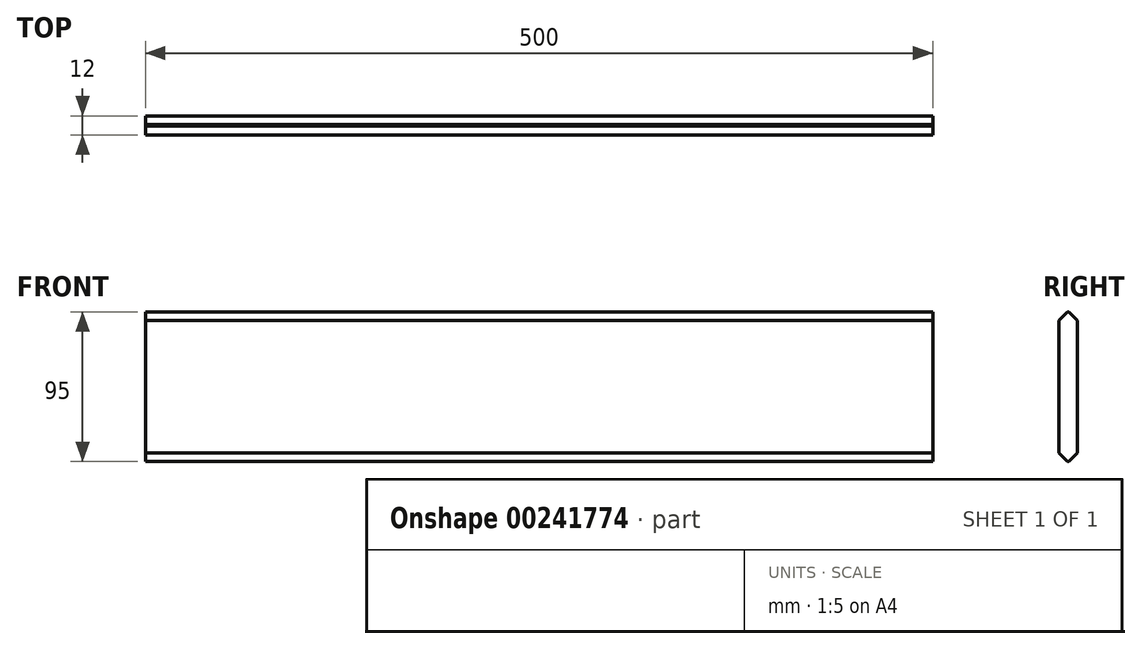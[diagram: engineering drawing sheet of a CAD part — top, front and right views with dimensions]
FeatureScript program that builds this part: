
annotation { "Feature Type Name" : "Feature", "Feature Type Description" : "" }
export const myFeature = defineFeature(function(context is Context, id is Id, definition is map)
    precondition{}
    {
        {
            var Q0;
            Q0=qCreatedBy(makeId("Front.planeOp"),FACE);
            var sketch = newSketch(context, id + "F0", { "sketchPlane" : qUnion([Q0])});
            skLineSegment(sketch, "E0.bottom", {"start": v(0, 0) * mm, "end": v(500, 0) * mm});
            skLineSegment(sketch, "E0.top", {"start": v(0, 95) * mm, "end": v(500, 95) * mm});
            skLineSegment(sketch, "E0.left", {"start": v(0, 0) * mm, "end": v(0, 95) * mm});
            skLineSegment(sketch, "E0.right", {"start": v(500, 0) * mm, "end": v(500, 95) * mm});
            skSolve(sketch);
        }
        {
            var Q0;
            Q0=qSketchRegion(id+"F0",true);
            extrude(context, id + "F1", {"entities" : qUnion([Q0]), "depth" : 12 * mm});
        }
        {
            var Q0;
            Q0=makeQuery(id+"F1.opExtrude","CAP_EDGE",EDGE,{"disambiguationData":[OSD([sQuery(id+"F0.wireOp",EDGE,"E0.top")])],"isStart":false});
            var Q1;
            Q1=makeQuery(id+"F1.opExtrude","CAP_EDGE",EDGE,{"disambiguationData":[OSD([sQuery(id+"F0.wireOp",EDGE,"E0.top")])],"isStart":true});
            var Q2;
            Q2=makeQuery(id+"F1.opExtrude","CAP_EDGE",EDGE,{"disambiguationData":[OSD([sQuery(id+"F0.wireOp",EDGE,"E0.bottom")])],"isStart":false});
            var Q3;
            Q3=makeQuery(id+"F1.opExtrude","CAP_EDGE",EDGE,{"disambiguationData":[OSD([sQuery(id+"F0.wireOp",EDGE,"E0.bottom")])],"isStart":true});
            chamfer(context, id + "F2", {"entities" : qUnion([Q0, Q1, Q2, Q3]), "width" : 5.5 * mm});
        }
    });
